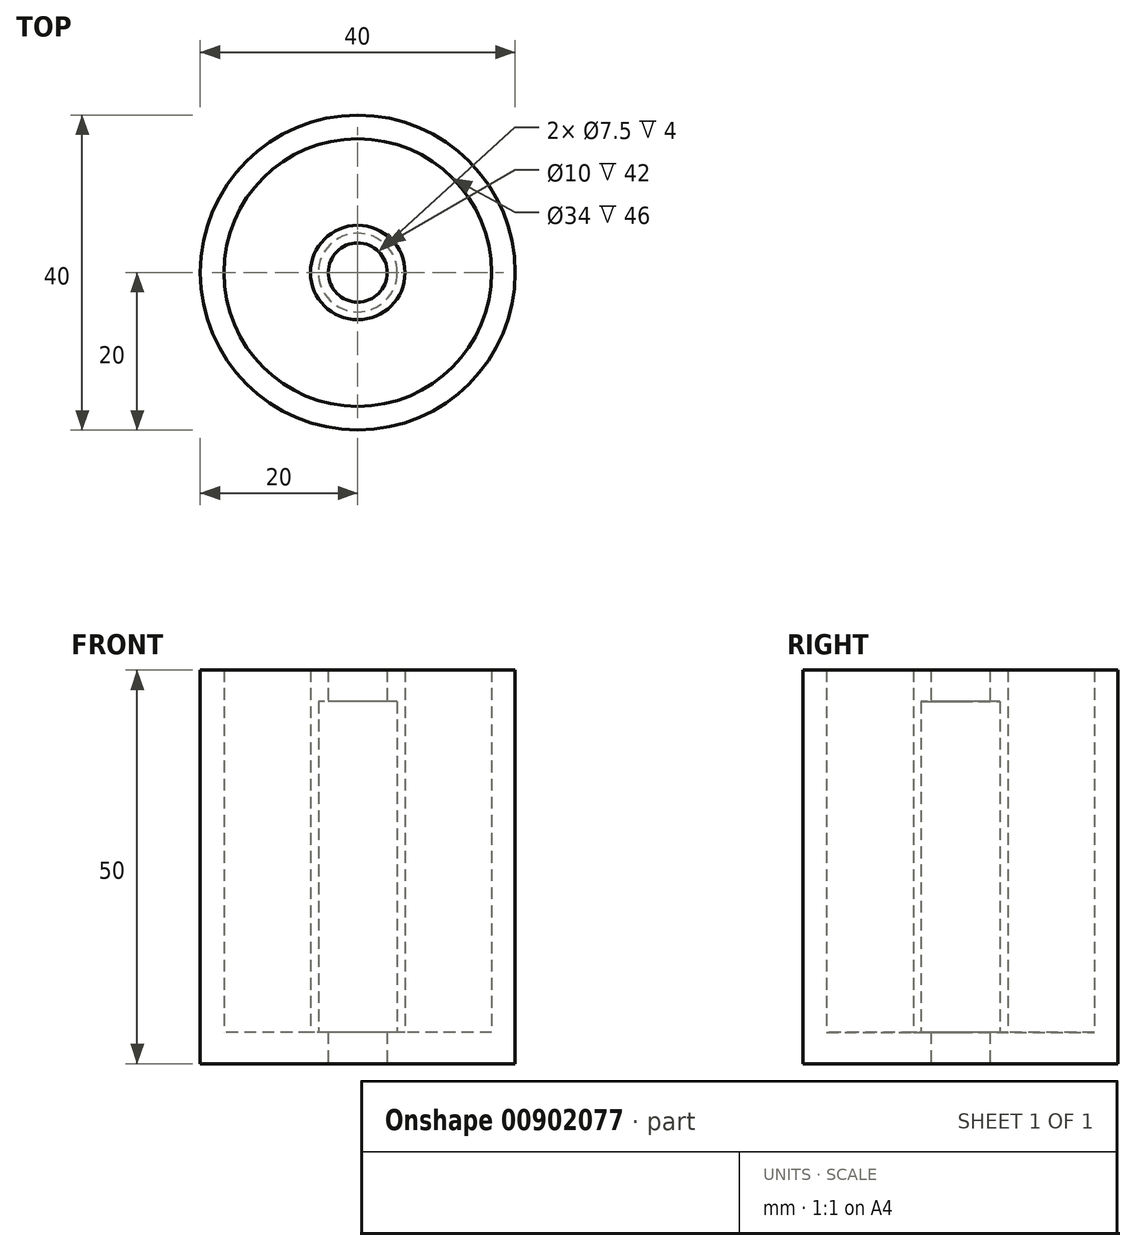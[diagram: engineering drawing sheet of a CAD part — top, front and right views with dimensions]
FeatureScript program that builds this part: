
annotation { "Feature Type Name" : "Feature", "Feature Type Description" : "" }
export const myFeature = defineFeature(function(context is Context, id is Id, definition is map)
    precondition{}
    {
        {
            var Q0;
            Q0=qCreatedBy(makeId("Top.planeOp"),FACE);
            var sketch = newSketch(context, id + "F0", { "sketchPlane" : qUnion([Q0])});
            skCircle(sketch, "E0", {"center": v(0, 0) * mm, "radius": 3.75 * mm});
            skCircle(sketch, "E1", {"center": v(0, 0) * mm, "radius": 5 * mm});
            skCircle(sketch, "E2", {"center": v(0, 0) * mm, "radius": 6 * mm});
            skSolve(sketch);
        }
        {
            var Q0;
            Q0=makeQuery(id+"F0.imprint","IMPRINT",FACE,{"disambiguationData":[TD([[makeQuery(id+"F0.imprint","IMPRINT",EDGE,{"derivedFrom":sQuery(id+"F0.wireOp",EDGE,"E1")}),-1.0]])]});
            var Q1;
            Q1=makeQuery(id+"F0.imprint","IMPRINT",FACE,{"disambiguationData":[TD([[makeQuery(id+"F0.imprint","IMPRINT",EDGE,{"derivedFrom":sQuery(id+"F0.wireOp",EDGE,"E0")}),-1.0]])]});
            extrude(context, id + "F1", {"entities" : qUnion([Q0, Q1]), "depth" : 4 * mm, "offsetDistance" : 25 * mm});
        }
        {
            var Q0;
            Q0=makeQuery(id+"F1.opExtrude","CAP_FACE",FACE,{"disambiguationData":[OSD([sQuery(id+"F0.wireOp",EDGE,"E0"),sQuery(id+"F0.wireOp",EDGE,"E2")])],"isStart":false});
            var sketch = newSketch(context, id + "F2", { "sketchPlane" : qUnion([Q0])});
            skCircle(sketch, "E3.0", {"center": v(0, 0) * mm, "radius": 5 * mm});
            skCircle(sketch, "E4.0", {"center": v(0, 0) * mm, "radius": 6 * mm});
            skSolve(sketch);
        }
        {
            var Q0;
            Q0=makeQuery(id+"F2.imprint","IMPRINT",FACE,{"disambiguationData":[TD([[makeQuery(id+"F2.imprint","IMPRINT",EDGE,{"derivedFrom":sQuery(id+"F2.wireOp",EDGE,"E3.0")}),-1.0]])]});
            extrude(context, id + "F3", {"entities" : qUnion([Q0]), "operationType" : NewBodyOperationType.ADD, "depth" : 42 * mm, "offsetDistance" : 25 * mm});
        }
        {
            var Q0;
            Q0=makeQuery(id+"F3.opExtrude","CAP_FACE",FACE,{"disambiguationData":[OSD([sQuery(id+"F2.wireOp",EDGE,"E3.0"),sQuery(id+"F2.wireOp",EDGE,"E4.0")])],"isStart":false});
            var sketch = newSketch(context, id + "F4", { "sketchPlane" : qUnion([Q0])});
            skCircle(sketch, "E5.0", {"center": v(0, 0) * mm, "radius": 3.75 * mm});
            skCircle(sketch, "E6.0", {"center": v(0, 0) * mm, "radius": 6 * mm});
            skSolve(sketch);
        }
        {
            var Q0;
            Q0=makeQuery(id+"F4.imprint","IMPRINT",FACE,{"disambiguationData":[TD([[makeQuery(id+"F4.imprint","IMPRINT",EDGE,{"derivedFrom":sQuery(id+"F4.wireOp",EDGE,"E5.0")}),-1.0]])]});
            var Q1;
            Q1=makeQuery(id+"F4.imprint","IMPRINT",FACE,{"disambiguationData":[TD([[makeQuery(id+"F4.imprint","IMPRINT",EDGE,{"derivedFrom":sQuery(id+"F4.wireOp",EDGE,"E6.0")}),1.0]])]});
            extrude(context, id + "F5", {"entities" : qUnion([Q0, Q1]), "operationType" : NewBodyOperationType.ADD, "depth" : 4 * mm, "offsetDistance" : 25 * mm});
        }
        {
            var Q0;
            Q0=makeQuery(id+"F0.imprint","IMPRINT",FACE,{"disambiguationData":[TD([[makeQuery(id+"F0.imprint","IMPRINT",EDGE,{"derivedFrom":sQuery(id+"F0.wireOp",EDGE,"E1")}),-1.0]])]});
            var Q1;
            Q1=makeQuery(id+"F0.imprint","IMPRINT",FACE,{"disambiguationData":[TD([[makeQuery(id+"F0.imprint","IMPRINT",EDGE,{"derivedFrom":sQuery(id+"F0.wireOp",EDGE,"E0")}),-1.0]])]});
            extrude(context, id + "F6", {"entities" : qUnion([Q0, Q1]), "depth" : 3 * mm, "offsetDistance" : 25 * mm});
        }
        {
            var Q0;
            Q0=qCreatedBy(makeId("Top.planeOp"),FACE);
            var sketch = newSketch(context, id + "F7", { "sketchPlane" : qUnion([Q0])});
            skCircle(sketch, "E7", {"center": v(0, 0) * mm, "radius": 20 * mm});
            skCircle(sketch, "E8.0", {"center": v(0, 0) * mm, "radius": 6 * mm});
            skSolve(sketch);
        }
        {
            var Q0;
            Q0=makeQuery(id+"F7.imprint","IMPRINT",FACE,{"disambiguationData":[TD([[makeQuery(id+"F7.imprint","IMPRINT",EDGE,{"derivedFrom":sQuery(id+"F7.wireOp",EDGE,"E7")}),1.0]])]});
            extrude(context, id + "F8", {"entities" : qUnion([Q0]), "operationType" : NewBodyOperationType.ADD, "depth" : 4 * mm, "offsetDistance" : 25 * mm});
        }
        {
            var Q0;
            Q0=makeQuery(id+"F8.opExtrude","CAP_FACE",FACE,{"disambiguationData":[OSD([sQuery(id+"F7.wireOp",EDGE,"E7"),sQuery(id+"F7.wireOp",EDGE,"E8.0")])],"isStart":false});
            var sketch = newSketch(context, id + "F9", { "sketchPlane" : qUnion([Q0])});
            skCircle(sketch, "E9.0", {"center": v(0, 0) * mm, "radius": 20 * mm});
            skCircle(sketch, "E10", {"center": v(0, 0) * mm, "radius": 17 * mm});
            skSolve(sketch);
        }
        {
            var Q0;
            Q0=makeQuery(id+"F9.imprint","IMPRINT",FACE,{"disambiguationData":[TD([[makeQuery(id+"F9.imprint","IMPRINT",EDGE,{"derivedFrom":sQuery(id+"F9.wireOp",EDGE,"E9.0")}),1.0]])]});
            extrude(context, id + "F10", {"entities" : qUnion([Q0]), "operationType" : NewBodyOperationType.ADD, "depth" : 46 * mm, "offsetDistance" : 25 * mm});
        }
    });
